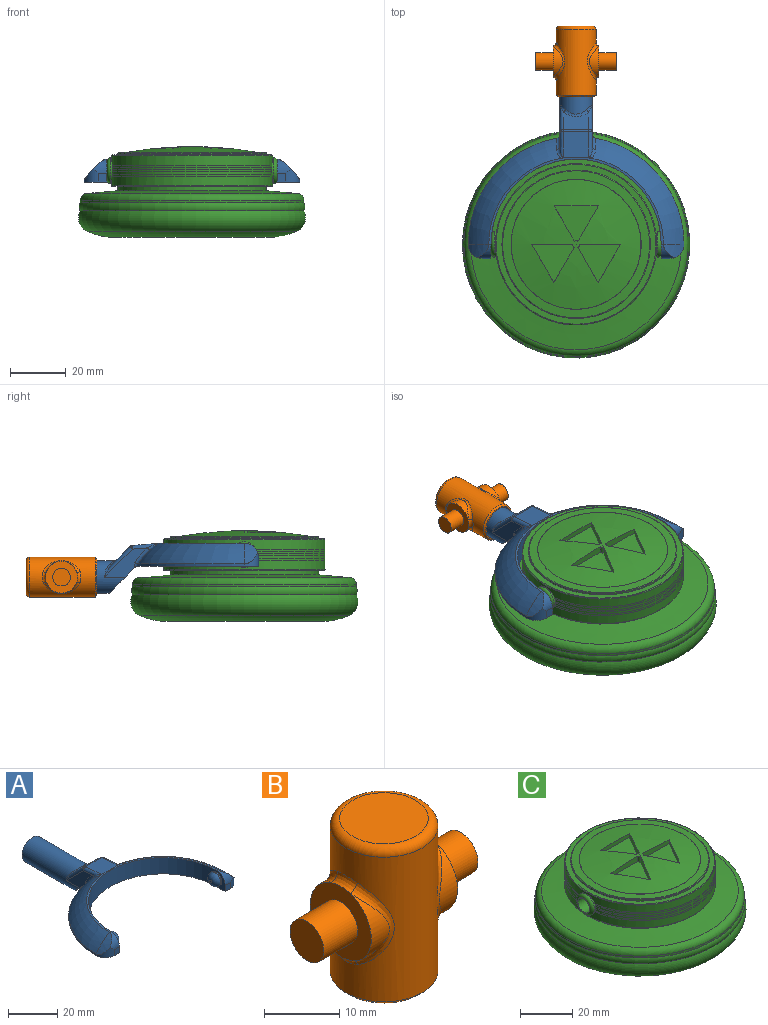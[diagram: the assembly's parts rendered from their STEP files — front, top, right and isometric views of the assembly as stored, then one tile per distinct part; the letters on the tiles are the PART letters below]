
ASSEMBLY  parts=3 mates=2
PART A: 48 faces, bbox 77.3x80.8x18.2 mm
  f0: plane 11.99x9.83mm, normal (0,-0.71,-0.71), area 141.5mm2, adj f1,f2,f9,f30,f43,f46
  f1: plane 15.39x10.49mm, normal (-1,0,0), area 63.5mm2, adj f0,f30,f32,f36,f46,f47
  f2: plane 15.39x10.49mm, normal (1,0,0), area 63.5mm2, adj f0,f30,f34,f39,f43,f44
  f3: plane 9.14x6.37mm, normal (0,0.71,0.71), area 67.6mm2, adj f35,f36,f39,f40
  f4: cylinder r=38.61mm len=37.99mm, axis (0,0,-1), area 42.6mm2, adj f6,f9,f17,f46,f47
  f5: torus R=19.3mm, axis (0,0,-1), area 507.8mm2, adj f10,f11,f12,f29,f42,f44
  f6: torus R=19.3mm, axis (0,0,-1), area 507.8mm2, adj f4,f11,f15,f28,f45,f47
  f7: cylinder r=30.48mm len=60.96mm, axis (0,0,-1), area 746.6mm2, adj f8,f9,f11,f14,f21,f24
  f8: plane 8.13x5.08mm, normal (-1,0,0), area 19.9mm2, adj f7,f9,f13,f19,f24
  f9: plane 77.22x43.73mm, normal (0,0,-1), area 956.2mm2, adj f0,f4,f7,f8,f10,f13,f14,f16
  f10: cylinder r=38.61mm len=37.99mm, axis (0,0,-1), area 42.6mm2, adj f5,f9,f20,f43,f44
  f11: plane 62.55x30.95mm, normal (0,0,1), area 75mm2, adj f5,f6,f7,f18,f19,f27
  f12: cylinder r=22.71mm len=7.33mm, axis (0,1,0), area 24.8mm2, adj f5,f19,f20
  f13: plane 3.05x3.05mm, normal (0,-1,0), area 9.3mm2, adj f8,f9,f19,f20
  f14: plane 8.13x5.08mm, normal (1,0,0), area 19.9mm2, adj f7,f9,f16,f18,f21
  f15: cylinder r=22.71mm len=7.33mm, axis (0,1,0), area 24.8mm2, adj f6,f17,f18
  f16: plane 3.05x3.05mm, normal (0,-1,0), area 9.3mm2, adj f9,f14,f17,f18
  f17: cylinder r=5.08mm len=5.08mm, axis (0,0,-1), area 21.9mm2, adj f4,f9,f15,f16,f18
  f18: cylinder r=5.08mm len=5.08mm, axis (-1,0,0), area 21.9mm2, adj f11,f14,f15,f16,f17
  f19: cylinder r=5.08mm len=5.08mm, axis (-1,0,0), area 21.9mm2, adj f8,f11,f12,f13,f20
  f20: cylinder r=5.08mm len=5.08mm, axis (0,0,-1), area 21.9mm2, adj f9,f10,f12,f13,f19
  f21: cylinder r=3.17mm len=6.35mm, axis (-1,0,0), area 12.7mm2, adj f7,f14,f23
  f22: plane 1.27x1.27mm, normal (1,0,0), area 1.3mm2, adj f23
  f23: torus R=0.64mm, axis (1,0,0), area 56.5mm2, adj f21,f22
  f24: cylinder r=3.17mm len=6.35mm, axis (1,0,0), area 12.7mm2, adj f7,f8,f26
  f25: plane 1.27x1.27mm, normal (-1,0,0), area 1.3mm2, adj f26
  f26: torus R=0.64mm, axis (-1,0,0), area 56.5mm2, adj f24,f25
  f27: plane 9.86x9.36mm, normal (0,0.09,1), area 85.6mm2, adj f11,f28,f29,f32,f34,f35,f42,f45
  f28: plane 1.04x0.17mm, normal (0,-1,0), area 0mm2, adj f6,f27,f45
  f29: plane 1.04x0.17mm, normal (0,-1,0), area 0mm2, adj f5,f27,f42
  f30: cylinder r=5.84mm len=33.01mm, axis (0,-1,0), area 1029.7mm2, adj f0,f1,f2,f31,f38,f40,f41
  f31: plane 11.68x11.68mm, normal (0,1,0), area 107.2mm2, adj f30
  f32: cylinder r=1.27mm len=9.13mm, axis (0,-1,0.09), area 14.4mm2, adj f1,f27,f33,f45
  f33: sphere r=1.27mm, area 1.5mm2, adj f32,f35,f36
  f34: cylinder r=1.27mm len=9.13mm, axis (0,1,-0.09), area 14.4mm2, adj f2,f27,f37,f42
  f35: cylinder r=1.27mm len=9.14mm, axis (-1,0,0), area 8.1mm2, adj f3,f27,f33,f37
  f36: cylinder r=1.27mm len=10.91mm, axis (0,-0.71,0.71), area 23.1mm2, adj f1,f3,f33,f38
  f37: sphere r=1.27mm, area 1.5mm2, adj f34,f35,f39
  f38: bspline ~4.55x2.75mm, area 2.3mm2, adj f30,f36,f40
  f39: cylinder r=1.27mm len=10.91mm, axis (0,0.71,-0.71), area 23.1mm2, adj f2,f3,f37,f41
  f40: bspline ~9.14x2.56mm, area 10.7mm2, adj f3,f30,f38,f41
  f41: bspline ~5.23x3.53mm, area 2.3mm2, adj f30,f39,f40
  f42: bspline ~4.62x3.14mm, area 5.2mm2, adj f5,f27,f29,f34,f44
  f43: cylinder r=1.27mm len=1.74mm, axis (0,0,-1), area 1.9mm2, adj f0,f2,f9,f10,f44
  f44: bspline ~8.6x7.86mm, area 11.9mm2, adj f2,f5,f10,f42,f43
  f45: bspline ~4.62x3.14mm, area 5.2mm2, adj f6,f27,f28,f32,f47
  f46: cylinder r=1.27mm len=1.74mm, axis (0,0,-1), area 1.9mm2, adj f0,f1,f4,f9,f47
  f47: bspline ~8.6x7.86mm, area 11.9mm2, adj f1,f4,f6,f45,f46
PART B: 25 faces, bbox 28.9x15.5x25.4 mm
  f0: cylinder r=5.71mm len=10.81mm, axis (-1,0,0), area 26.2mm2, adj f5,f15
  f1: cylinder r=5.71mm len=10.81mm, axis (-1,0,0), area 26.2mm2, adj f8,f11
  f2: cylinder r=7.14mm len=23.5mm, axis (0,0,-1), area 763.2mm2, adj f9,f10,f11,f12,f13,f14,f15,f16
  f3: plane 11.75x11.75mm, normal (0,0,1), area 108.4mm2, adj f17
  f4: plane 13.02x13.02mm, normal (0,0,-1), area 16.3mm2, adj f22,f24
  f5: plane 11.46x11.46mm, normal (1,0,0), area 70.9mm2, adj f0,f6,f13,f16,f18
  f6: cylinder r=5.71mm len=10.81mm, axis (-1,0,0), area 26.2mm2, adj f5,f14
  f7: cylinder r=5.71mm len=10.81mm, axis (-1,0,0), area 26.2mm2, adj f8,f10
  f8: plane 11.46x11.46mm, normal (-1,0,0), area 70.9mm2, adj f1,f7,f9,f12,f20
  f9: bspline ~4.64x1.73mm, area 6.5mm2, adj f2,f8,f10,f11
  f10: bspline ~13.62x4.91mm, area 20.7mm2, adj f2,f7,f9,f12
  f11: bspline ~13.6x4.87mm, area 20.7mm2, adj f1,f2,f9,f12
  f12: bspline ~4.64x1.73mm, area 6.5mm2, adj f2,f8,f10,f11
  f13: bspline ~4.64x1.73mm, area 6.5mm2, adj f2,f5,f14,f15
  f14: bspline ~13.62x4.91mm, area 20.7mm2, adj f2,f6,f13,f16
  f15: bspline ~13.6x4.87mm, area 20.7mm2, adj f0,f2,f13,f16
  f16: bspline ~4.64x1.73mm, area 6.5mm2, adj f2,f5,f14,f15
  f17: torus R=5.87mm, axis (0,0,1), area 83.8mm2, adj f2,f3
  f18: cylinder r=3.17mm len=6.35mm, axis (-1,0,0), area 126.7mm2, adj f5,f19
  f19: plane 6.35x6.35mm, normal (1,0,0), area 31.7mm2, adj f18
  f20: cylinder r=3.17mm len=6.35mm, axis (1,0,0), area 126.7mm2, adj f8,f21
  f21: plane 6.35x6.35mm, normal (-1,0,0), area 31.7mm2, adj f20
  f22: cylinder r=6.1mm len=22.86mm, axis (0,0,-1), area 875.6mm2, adj f4,f23
  f23: plane 12.19x12.19mm, normal (0,0,-1), area 116.7mm2, adj f22
  f24: cone r=7.14mm half-angle=45deg, axis (0,0,1), area 38.5mm2, adj f2,f4
PART C: 77 faces, bbox 96.2x96.2x32.5 mm
  f0: cylinder r=28.87mm len=57.73mm, axis (0,0,-1), area 1814.4mm2, adj f31,f32,f37,f38
  f1: sphere r=135.39mm, area 1385.3mm2, adj f15,f16,f17,f18,f20,f21,f22,f23
  f2: plane 39.33x39.33mm, normal (0,0,-1), area 1214.6mm2, adj f3
  f3: torus R=20.12mm, axis (0,0,-1), area 1429.3mm2, adj f2,f4
  f4: torus R=27.74mm, axis (0,0,-1), area 3542.1mm2, adj f3,f5
  f5: torus R=35.36mm, axis (0,0,-1), area 2180.1mm2, adj f4,f6
  f6: torus R=37.35mm, axis (0,0,-1), area 734.6mm2, adj f5,f7
  f7: cylinder r=40.06mm len=80.11mm, axis (0,0,-1), area 213.3mm2, adj f6,f14
  f8: cone r=26.57mm half-angle=85deg, axis (0,0,-1), area 2265mm2, adj f9,f14
  f9: cylinder r=26.57mm len=53.14mm, axis (0,0,-1), area 265mm2, adj f8,f10
  f10: plane 57.23x57.23mm, normal (0,0,-1), area 354.5mm2, adj f9,f37
  f11: plane 57.23x57.23mm, normal (0,0,1), area 354.5mm2, adj f12,f38
  f12: cylinder r=26.57mm len=53.14mm, axis (0,0,-1), area 92.3mm2, adj f11,f39
  f13: cone r=26.57mm half-angle=87deg, axis (0,0,-1), area 475.4mm2, adj f39,f40
  f14: torus R=37.52mm, axis (0,0,1), area 928.6mm2, adj f7,f8
  f15: plane 13.78x7.88mm, normal (0.87,0.5,0), area 28mm2, adj f1,f16,f18,f19
  f16: plane 12.62x7.35mm, normal (-0.86,0.5,0), area 32.2mm2, adj f1,f15,f17,f19
  f17: cylinder r=1.27mm len=2.53mm, axis (0,0,1), area 3.4mm2, adj f1,f16,f18,f19
  f18: plane 14.61x2.53mm, normal (0,-1,0), area 32.2mm2, adj f1,f15,f17,f19
  f19: plane 15.24x13.78mm, normal (0,0,1), area 108.3mm2, adj f15,f16,f17,f18
  f20: plane 12.68x7.25mm, normal (0.87,0.5,0), area 32.2mm2, adj f1,f21,f23,f24
  f21: plane 13.72x7.99mm, normal (-0.86,0.5,0), area 28mm2, adj f1,f20,f22,f24
  f22: plane 14.61x2.53mm, normal (0,-1,0), area 32.2mm2, adj f1,f21,f23,f24
  f23: cylinder r=1.27mm len=2.53mm, axis (0,0,1), area 3.4mm2, adj f1,f20,f22,f24
  f24: plane 15.24x13.77mm, normal (0,0,1), area 108.3mm2, adj f20,f21,f22,f23
  f25: cylinder r=1.27mm len=2.53mm, axis (0,0,1), area 3.4mm2, adj f1,f26,f28,f29
  f26: plane 12.62x7.35mm, normal (-0.86,0.5,0), area 32.2mm2, adj f1,f25,f27,f29
  f27: plane 15.88x1.84mm, normal (0,-1,0), area 28mm2, adj f1,f26,f28,f29
  f28: plane 12.68x7.25mm, normal (0.87,0.5,0), area 32.2mm2, adj f1,f25,f27,f29
  f29: plane 15.88x12.68mm, normal (0,0,1), area 108.3mm2, adj f25,f26,f27,f28
  f30: plane 6.6x6.6mm, normal (1,0,0), area 2.6mm2, adj f35,f36
  f31: cylinder r=4.57mm len=9.14mm, axis (-1,0,0), area 15.1mm2, adj f0,f35
  f32: cylinder r=4.57mm len=9.14mm, axis (-1,0,0), area 15.1mm2, adj f0,f34
  f33: plane 6.6x6.6mm, normal (-1,0,0), area 2.6mm2, adj f34,f36
  f34: torus R=3.3mm, axis (1,0,0), area 51.5mm2, adj f32,f33
  f35: torus R=3.3mm, axis (1,0,0), area 51.5mm2, adj f30,f31
  f36: cylinder r=3.17mm len=60.96mm, axis (1,0,0), area 1216.1mm2, adj f30,f33
  f37: torus R=28.61mm, axis (0,0,1), area 72.1mm2, adj f0,f10
  f38: torus R=28.61mm, axis (0,0,-1), area 72.1mm2, adj f0,f11
  f39: torus R=26.31mm, axis (0,0,1), area 64.2mm2, adj f12,f13
  f40: torus R=23.29mm, axis (0,0,1), area 4.5mm2, adj f1,f13
  f41: cylinder r=4.57mm len=1.32mm, axis (-1,0,0), area 0.9mm2, adj f42,f43,f44,f45
  f42: cylinder r=27.58mm len=54.53mm, axis (0,0,-1), area 49.6mm2, adj f41,f43,f45,f46
  f43: plane 57.03x24.46mm, normal (0,0,1), area 101.4mm2, adj f41,f42,f44,f46
  f44: cylinder r=28.85mm len=57.1mm, axis (0,0,-1), area 52.1mm2, adj f41,f43,f45,f46
  f45: plane 57.1x24.7mm, normal (0,0,-1), area 102mm2, adj f41,f42,f44,f46
  f46: cylinder r=4.57mm len=1.32mm, axis (-1,0,0), area 0.9mm2, adj f42,f43,f44,f45
  f47: cylinder r=4.57mm len=1.32mm, axis (-1,0,0), area 0.9mm2, adj f48,f49,f50,f51
  f48: cylinder r=27.58mm len=54.53mm, axis (0,0,-1), area 49.6mm2, adj f47,f49,f51,f52
  f49: plane 57.1x24.7mm, normal (0,0,1), area 102mm2, adj f47,f48,f50,f52
  f50: cylinder r=28.85mm len=57.1mm, axis (0,0,-1), area 52.1mm2, adj f47,f49,f51,f52
  f51: plane 57.03x24.46mm, normal (0,0,-1), area 101.4mm2, adj f47,f48,f50,f52
  f52: cylinder r=4.57mm len=1.32mm, axis (-1,0,0), area 0.9mm2, adj f48,f49,f50,f51
  f53: cylinder r=4.57mm len=1.29mm, axis (-1,0,0), area 0.8mm2, adj f54,f55,f56,f57
  f54: cylinder r=27.58mm len=54.4mm, axis (0,0,-1), area 49.2mm2, adj f53,f55,f57,f58
  f55: plane 56.98x24.29mm, normal (0,0,1), area 100.9mm2, adj f53,f54,f56,f58
  f56: cylinder r=28.85mm len=56.98mm, axis (0,0,-1), area 51.7mm2, adj f53,f55,f57,f58
  f57: plane 56.98x24.29mm, normal (0,0,-1), area 100.9mm2, adj f53,f54,f56,f58
  f58: cylinder r=4.57mm len=1.29mm, axis (-1,0,0), area 0.8mm2, adj f54,f55,f56,f57
  f59: plane 57.1x24.7mm, normal (0,0,-1), area 102mm2, adj f60,f62,f63,f64
  f60: cylinder r=28.85mm len=57.1mm, axis (0,0,-1), area 52.1mm2, adj f59,f61,f63,f64
  f61: plane 57.03x24.46mm, normal (0,0,1), area 101.4mm2, adj f60,f62,f63,f64
  f62: cylinder r=27.58mm len=54.53mm, axis (0,0,-1), area 49.6mm2, adj f59,f61,f63,f64
  f63: cylinder r=4.57mm len=1.32mm, axis (-1,0,0), area 0.9mm2, adj f59,f60,f61,f62
  f64: cylinder r=4.57mm len=1.32mm, axis (-1,0,0), area 0.9mm2, adj f59,f60,f61,f62
  f65: plane 57.03x24.46mm, normal (0,0,-1), area 101.4mm2, adj f66,f68,f69,f70
  f66: cylinder r=28.85mm len=57.1mm, axis (0,0,-1), area 52.1mm2, adj f65,f67,f69,f70
  f67: plane 57.1x24.7mm, normal (0,0,1), area 102mm2, adj f66,f68,f69,f70
  f68: cylinder r=27.58mm len=54.53mm, axis (0,0,-1), area 49.6mm2, adj f65,f67,f69,f70
  f69: cylinder r=4.57mm len=1.32mm, axis (-1,0,0), area 0.9mm2, adj f65,f66,f67,f68
  f70: cylinder r=4.57mm len=1.32mm, axis (-1,0,0), area 0.9mm2, adj f65,f66,f67,f68
  f71: plane 56.98x24.29mm, normal (0,0,-1), area 100.9mm2, adj f72,f74,f75,f76
  f72: cylinder r=28.85mm len=56.98mm, axis (0,0,-1), area 51.7mm2, adj f71,f73,f75,f76
  f73: plane 56.98x24.29mm, normal (0,0,1), area 100.9mm2, adj f72,f74,f75,f76
  f74: cylinder r=27.58mm len=54.4mm, axis (0,0,-1), area 49.2mm2, adj f71,f73,f75,f76
  f75: cylinder r=4.57mm len=1.29mm, axis (-1,0,0), area 0.8mm2, adj f71,f72,f73,f74
  f76: cylinder r=4.57mm len=1.29mm, axis (-1,0,0), area 0.8mm2, adj f71,f72,f73,f74
PLACE A t=(32.34,27.52,20.85)mm
PLACE B rot(axis=(-1,0,0),90deg) t=(32.34,80.3,16.88)mm
PLACE C t=(32.34,27.52,33.52)mm
MATE revolute A.f24 <-> C.f31  axis (-1,0,0) through (62.82,27.52,24.92)mm
MATE revolute B.f2 <-> A.f30  axis (0,-1,0) through (32.34,103.16,16.88)mm
